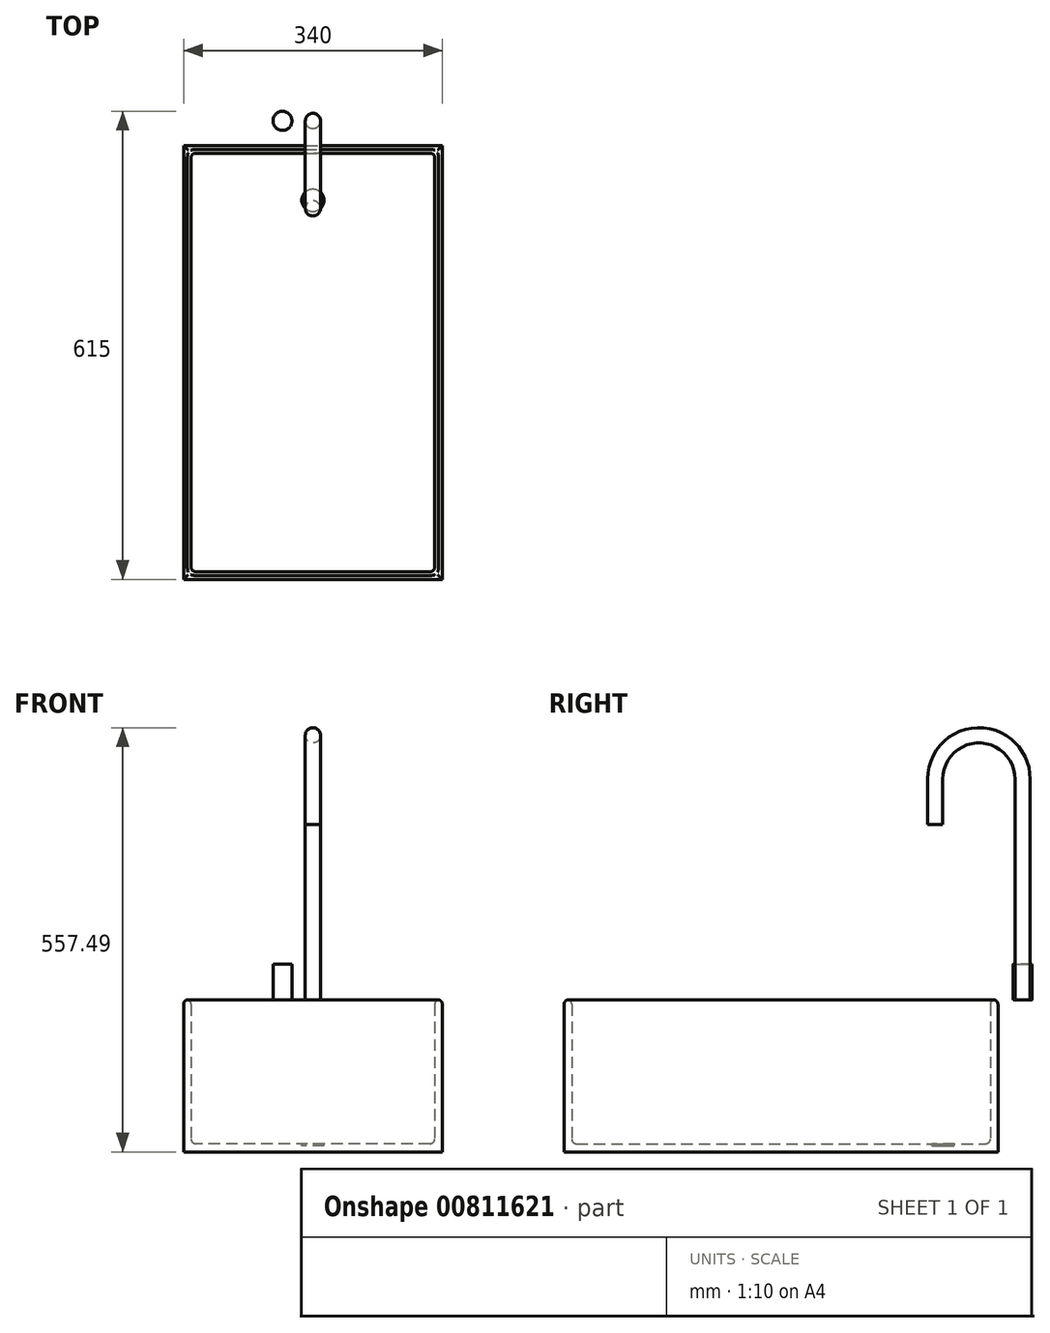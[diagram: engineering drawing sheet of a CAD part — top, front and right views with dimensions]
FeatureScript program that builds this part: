
annotation { "Feature Type Name" : "Feature", "Feature Type Description" : "" }
export const myFeature = defineFeature(function(context is Context, id is Id, definition is map)
    precondition{}
    {
        {
            var Q0;
            Q0=qCreatedBy(makeId("Top.planeOp"),FACE);
            var sketch = newSketch(context, id + "F0", { "sketchPlane" : qUnion([Q0])});
            skLineSegment(sketch, "E0.bottom", {"start": v(-17.58, 539.68) * mm, "end": v(322.42, 539.68) * mm});
            skLineSegment(sketch, "E0.top", {"start": v(-17.58, -30.32) * mm, "end": v(322.42, -30.32) * mm});
            skLineSegment(sketch, "E0.left", {"start": v(-17.58, 539.68) * mm, "end": v(-17.58, -30.32) * mm});
            skLineSegment(sketch, "E0.right", {"start": v(322.42, 539.68) * mm, "end": v(322.42, -30.32) * mm});
            skLineSegment(sketch, "E1.0", {"start": v(-7.58, 529.68) * mm, "end": v(312.42, 529.68) * mm});
            skLineSegment(sketch, "E1.1", {"start": v(-7.58, 529.68) * mm, "end": v(-7.58, -20.32) * mm});
            skLineSegment(sketch, "E1.2", {"start": v(-7.58, -20.32) * mm, "end": v(312.42, -20.32) * mm});
            skLineSegment(sketch, "E1.3", {"start": v(312.42, 529.68) * mm, "end": v(312.42, -20.32) * mm});
            skSolve(sketch);
        }
        {
            var Q0;
            Q0=qSketchRegion(id+"F0",true);
            extrude(context, id + "F1", {"entities" : qUnion([Q0]), "depth" : 200 * mm});
        }
        {
            var Q0;
            Q0=makeQuery(id+"F1.opExtrude","SWEPT_FACE",FACE,{"disambiguationData":[OSD([sQuery(id+"F0.wireOp",EDGE,"E0.top")])]});
            var sketch = newSketch(context, id + "F2", { "sketchPlane" : qUnion([Q0])});
            skLineSegment(sketch, "E2.bottom", {"start": v(-17.58, 0) * mm, "end": v(322.42, 0) * mm});
            skLineSegment(sketch, "E2.top", {"start": v(-17.58, 10.82) * mm, "end": v(322.42, 10.82) * mm});
            skLineSegment(sketch, "E2.left", {"start": v(-17.58, 0) * mm, "end": v(-17.58, 10.82) * mm});
            skLineSegment(sketch, "E2.right", {"start": v(322.42, 0) * mm, "end": v(322.42, 10.82) * mm});
            skSolve(sketch);
        }
        {
            var Q0;
            Q0=qSketchRegion(id+"F2",true);
            var Q1;
            Q1=makeQuery(id+"F1.opExtrude","SWEPT_FACE",FACE,{"disambiguationData":[OSD([sQuery(id+"F0.wireOp",EDGE,"E0.bottom")])]});
            extrude(context, id + "F3", {"entities" : qUnion([Q0]), "operationType" : NewBodyOperationType.ADD, "endBound" : BoundingType.UP_TO_SURFACE, "oppositeDirection" : true, "endBoundEntityFace" : qUnion([Q1]), "depth" : 25 * mm});
        }
        {
            var Q0;
            Q0=makeQuery(id+"F1.opExtrude","CAP_FACE",FACE,{"disambiguationData":[OSD([sQuery(id+"F0.wireOp",EDGE,"E0.bottom"),sQuery(id+"F0.wireOp",EDGE,"E0.top"),sQuery(id+"F0.wireOp",EDGE,"E0.left"),sQuery(id+"F0.wireOp",EDGE,"E0.right"),sQuery(id+"F0.wireOp",EDGE,"E1.0"),sQuery(id+"F0.wireOp",EDGE,"E1.1"),sQuery(id+"F0.wireOp",EDGE,"E1.2"),sQuery(id+"F0.wireOp",EDGE,"E1.3")])],"isStart":false});
            var Q1;
            Q1=makeQuery(id+"F3.opExtrude","SWEPT_FACE",FACE,{"disambiguationData":[OSD([sQuery(id+"F2.wireOp",EDGE,"E2.top")])]});
            var Q2;
            Q2=makeQuery(id+"F1.opExtrude","SWEPT_FACE",FACE,{"disambiguationData":[OSD([sQuery(id+"F0.wireOp",EDGE,"E1.0")])]});
            var Q3;
            Q3=makeQuery(id+"F1.opExtrude","SWEPT_EDGE",EDGE,{"disambiguationData":[OSD([sQuery(id+"F0.wireOp",EDGE,"E1.0"),sQuery(id+"F0.wireOp",EDGE,"E1.3")])]});
            var Q4;
            Q4=makeQuery(id+"F1.opExtrude","SWEPT_FACE",FACE,{"disambiguationData":[OSD([sQuery(id+"F0.wireOp",EDGE,"E1.2")])]});
            fillet(context, id + "F4", {"entities" : qUnion([Q0, Q1, Q2, Q3, Q4]), "radius" : 6 * mm, "tangentPropagation" : true, "allowEdgeOverflow" : false});
        }
        {
            var Q0;
            Q0=makeQuery(id+"F3.opExtrude","SWEPT_FACE",FACE,{"disambiguationData":[OSD([sQuery(id+"F2.wireOp",EDGE,"E2.top")])]});
            var sketch = newSketch(context, id + "F5", { "sketchPlane" : qUnion([Q0])});
            skCircle(sketch, "E3", {"center": v(152.42, 467.76) * mm, "radius": 14.59 * mm});
            skPoint(sketch, "E4.orphan", {"position": v(-1.58, 523.68) * mm});
            skPoint(sketch, "E5.end.orphan", {"position": v(306.42, -14.32) * mm});
            skPoint(sketch, "E6.start.orphan", {"position": v(152.42, 254.68) * mm});
            skSolve(sketch);
        }
        {
            var Q0;
            Q0=qSketchRegion(id+"F5",true);
            extrude(context, id + "F6", {"entities" : qUnion([Q0]), "operationType" : NewBodyOperationType.REMOVE, "oppositeDirection" : true, "depth" : 3 * mm});
        }
        {
            var Q0;
            Q0=qCreatedBy(makeId("Top.planeOp"),FACE);
            cPlane(context, id + "F7", {"entities" : qUnion([Q0]), "cplaneType" : CPlaneType.OFFSET, "offset" : 200 * mm, "width" : 150 * mm, "height" : 150 * mm});
        }
        {
            var Q0;
            Q0=qCreatedBy(id+"F7.planeOp",FACE);
            var sketch = newSketch(context, id + "F8", { "sketchPlane" : qUnion([Q0])});
            skLineSegment(sketch, "E7.0", {"start": v(-17.58, 539.68) * mm, "end": v(322.42, 539.68) * mm});
            skLineSegment(sketch, "E8", {"start": v(152.42, 539.68) * mm, "end": v(152.42, 604.68) * mm});
            skCircle(sketch, "E9", {"center": v(152.42, 572.18) * mm, "radius": 10 * mm});
            skSolve(sketch);
        }
        {
            var Q0;
            Q0=sQuery(id+"F8.wireOp",EDGE,"E8");
            cPlane(context, id + "F9", {"entities" : qUnion([Q0]), "cplaneType" : CPlaneType.LINE_ANGLE, "offset" : 25 * mm, "angle" : 90 * degree, "width" : 150 * mm, "height" : 150 * mm});
        }
        {
            var Q0;
            Q0=qCreatedBy(id+"F9.planeOp",FACE);
            var sketch = newSketch(context, id + "F10", { "sketchPlane" : qUnion([Q0])});
            skLineSegment(sketch, "E10.0", {"start": v(562.18, 200) * mm, "end": v(582.18, 200) * mm});
            skLineSegment(sketch, "E11", {"start": v(572.18, 200) * mm, "end": v(572.18, 430) * mm});
            skLineSegment(sketch, "E12", {"start": v(457.19, 430) * mm, "end": v(457.19, 490) * mm});
            skLineSegment(sketch, "E13", {"start": v(572.18, 430) * mm, "end": v(572.18, 490) * mm});
            skArc(sketch, "E14", {"start": v(572.18, 490) * mm, "mid": v(514.68, 547.5) * mm, "end": v(457.19, 490) * mm});
            skSolve(sketch);
        }
        {
            var Q0;
            Q0=qSketchRegion(id+"F8",true);
            var Q1;
            Q1=sQuery(id+"F10.wireOp",EDGE,"E11");
            var Q2;
            Q2=sQuery(id+"F10.wireOp",EDGE,"E13");
            var Q3;
            Q3=sQuery(id+"F10.wireOp",EDGE,"E14");
            var Q4;
            Q4=sQuery(id+"F10.wireOp",EDGE,"E12");
            sweep(context, id + "F11", {"profiles" : qUnion([Q0]), "path" : qUnion([Q1, Q2, Q3, Q4])});
        }
        {
            var Q0;
            Q0=qCreatedBy(id+"F7.planeOp",FACE);
            var sketch = newSketch(context, id + "F12", { "sketchPlane" : qUnion([Q0])});
            skCircle(sketch, "E15.0", {"center": v(152.42, 572.18) * mm, "radius": 10 * mm});
            skLineSegment(sketch, "E16", {"start": v(152.42, 572.18) * mm, "end": v(112.42, 572.18) * mm});
            skCircle(sketch, "E17", {"center": v(112.42, 572.18) * mm, "radius": 12.5 * mm});
            skLineSegment(sketch, "E18", {"start": v(152.42, 572.18) * mm, "end": v(152.42, 607.52) * mm});
            skCircle(sketch, "E19.MirrorC", {"center": v(192.42, 572.18) * mm, "radius": 12.5 * mm});
            skSolve(sketch);
        }
        {
            var Q0;
            Q0=makeQuery(id+"F12.imprint","IMPRINT",FACE,{"disambiguationData":[TD([[makeQuery(id+"F12.imprint","IMPRINT",EDGE,{"derivedFrom":sQuery(id+"F12.wireOp",EDGE,"E17")}),1.0]])]});
            var Q1;
            Q1=makeQuery(id+"F12.imprint","IMPRINT",FACE,{"disambiguationData":[TD([[makeQuery(id+"F12.imprint","IMPRINT",EDGE,{"derivedFrom":sQuery(id+"F12.wireOp",EDGE,"E19.MirrorC")}),-1.0]])]});
            extrude(context, id + "F13", {"entities" : qUnion([Q0, Q1]), "depth" : 47 * mm});
        }
    });
